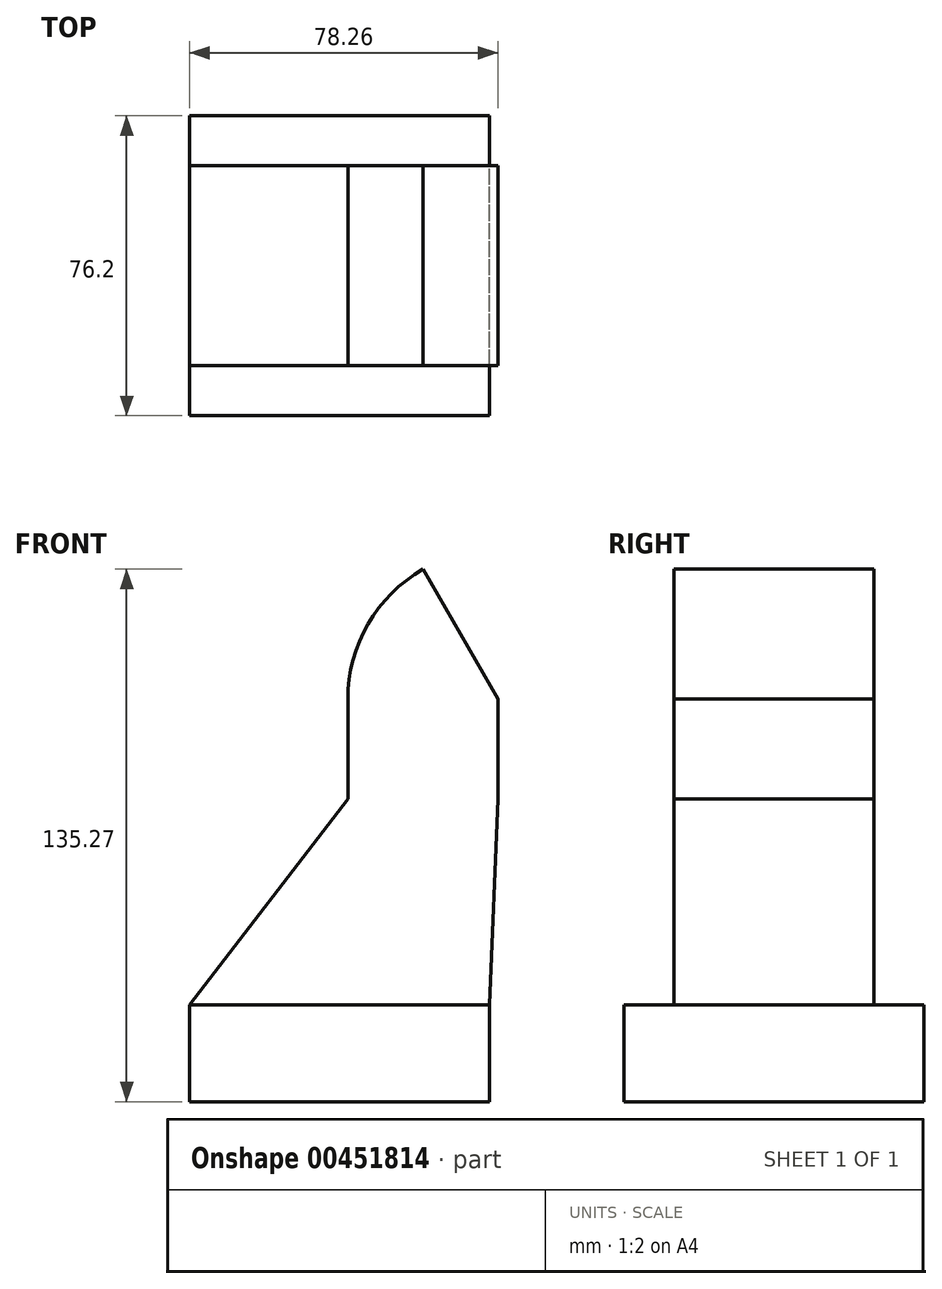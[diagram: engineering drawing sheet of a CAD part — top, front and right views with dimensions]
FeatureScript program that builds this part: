
annotation { "Feature Type Name" : "Feature", "Feature Type Description" : "" }
export const myFeature = defineFeature(function(context is Context, id is Id, definition is map)
    precondition{}
    {
        {
            var Q0;
            Q0=qCreatedBy(makeId("Front.planeOp"),FACE);
            var sketch = newSketch(context, id + "F0", { "sketchPlane" : qUnion([Q0])});
            skLineSegment(sketch, "E0.bottom", {"start": v(37.84, -12.31) * mm, "end": v(-38.36, -12.31) * mm});
            skLineSegment(sketch, "E0.top", {"start": v(37.84, 12.31) * mm, "end": v(-38.36, 12.31) * mm});
            skLineSegment(sketch, "E0.left", {"start": v(37.84, -12.31) * mm, "end": v(37.84, 12.31) * mm});
            skLineSegment(sketch, "E0.right", {"start": v(-38.36, -12.31) * mm, "end": v(-38.36, 12.31) * mm});
            skPoint(sketch, "E0.middle", {"position": v(-0.26, 0) * mm});
            skLineSegment(sketch, "E1.bottom", {"start": v(39.9, 64.57) * mm, "end": v(1.8, 64.57) * mm});
            skLineSegment(sketch, "E1.top", {"start": v(39.9, 89.97) * mm, "end": v(1.8, 89.97) * mm});
            skLineSegment(sketch, "E1.left", {"start": v(39.9, 64.57) * mm, "end": v(39.9, 89.97) * mm});
            skLineSegment(sketch, "E1.right", {"start": v(1.8, 64.57) * mm, "end": v(1.8, 89.97) * mm});
            skPoint(sketch, "E1.middle", {"position": v(20.85, 77.27) * mm});
            skLineSegment(sketch, "E2", {"start": v(-38.36, 12.31) * mm, "end": v(1.8, 64.57) * mm});
            skLineSegment(sketch, "E3", {"start": v(37.84, 12.31) * mm, "end": v(39.9, 64.57) * mm});
            skSolve(sketch);
        }
        {
            var Q0;
            Q0=makeQuery(id+"F0.imprint","IMPRINT",FACE,{"disambiguationData":[TD([[makeQuery(id+"F0.imprint","IMPRINT",EDGE,{"derivedFrom":sQuery(id+"F0.wireOp",EDGE,"E0.bottom")}),-1.0]])]});
            extrude(context, id + "F1", {"entities" : qUnion([Q0]), "endBound" : BoundingType.SYMMETRIC, "depth" : 76.2 * mm});
        }
        {
            var Q0;
            Q0 = qSketchRegion(id + "F0", true);
            extrude(context, id + "F2", {"entities" : qUnion([Q0]), "operationType" : NewBodyOperationType.ADD, "endBound" : BoundingType.SYMMETRIC, "depth" : 50.8 * mm});
        }
        {
            var Q0;
            Q0=makeQuery(id+"F2.opExtrude","SWEPT_FACE",FACE,{"disambiguationData":[OSD([sQuery(id+"F0.wireOp",EDGE,"E1.top")])]});
            var Q1;
            Q1=makeQuery(id+"F2.opExtrude","SWEPT_EDGE",EDGE,{"disambiguationData":[OSD([sQuery(id+"F0.wireOp",EDGE,"E1.top"),sQuery(id+"F0.wireOp",EDGE,"E1.left")])]});
            revolve(context, id + "F3", {"operationType" : NewBodyOperationType.ADD, "entities" : qUnion([Q0]), "axis" : qUnion([Q1]), "revolveType" : RevolveType.ONE_DIRECTION, "angle" : 60 * degree});
        }
    });
